# Revit family: COTTO-หัวฝักบัวก้านแข็งขนาด 12 นิ้ว สีทอง-Z98SV#GR2
name_source: partatom
category: Plumbing Fixtures
revit_build: Autodesk Revit 2017 (Build: 20160720_1515(x64)
units: mm (PartAtom-declared; Revit-internal decimal feet)

## family parameters
Always vertical = Yes
Cut with Voids When Loaded = No
Part Type = Normal
Room Calculation Point = No
Round Connector Dimension = Use Diameter
Shared = No
Work Plane-Based = No

## types (1)
- COTTO-หัวฝักบัวก้านแข็งขนาด 12 นิ้ว สีทอง-Z98SV#GR2
    Barcode = 8852410909402
    CW Connection = No
    Code = Z98SV#GR2
    Color = สีทอง
    Description = หัวฝักบัวก้านแข็งขนาด 12 นิ้ว สีทอง
    Drain = 0 mm  [stored 0 ft]
    Manufacturer = COTTO
    Material = SCG สแตนเลส SUS304
    Sap Code = Z234Z98SVGR2XXXX19
    Standard = มอก. 2066-2552
    URL = https://www.cotto.com
    Waste Connection = No
    Water Supply = 0 mm  [stored 0 ft]
    กว้าง (มม.) = 30 mm
    ยาว (มม.) = 5 mm  [stored 0.0164042 ft]
    สูง (มม.) = 30 mm
    แรงดันน้ำ = 3 บาร์

note: [stored X ft] marks values corroborated as IEEE doubles in the binary element streams (Revit-internal decimal feet)

## geometry (parser evidence)
native form markers: Sweep x3
no freeform markers — native parametric forms only
